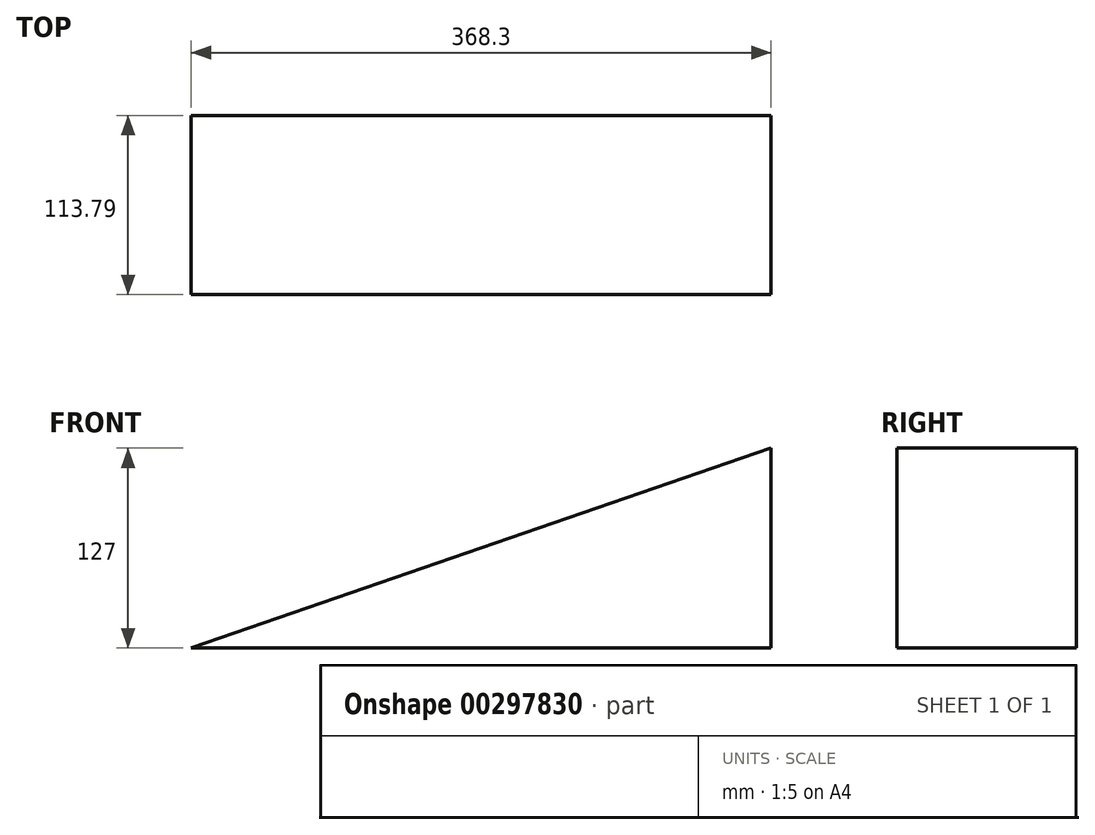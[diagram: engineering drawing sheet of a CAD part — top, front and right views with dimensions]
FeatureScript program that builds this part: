
annotation { "Feature Type Name" : "Feature", "Feature Type Description" : "" }
export const myFeature = defineFeature(function(context is Context, id is Id, definition is map)
    precondition{}
    {
        {
            var Q0;
            Q0=qCreatedBy(makeId("Front.planeOp"),FACE);
            var sketch = newSketch(context, id + "F0", { "sketchPlane" : qUnion([Q0])});
            skLineSegment(sketch, "E0", {"start": v(0, 0) * mm, "end": v(-368.3, 0) * mm});
            skLineSegment(sketch, "E1", {"start": v(0, 0) * mm, "end": v(0, 127) * mm});
            skLineSegment(sketch, "E2", {"start": v(0, 127) * mm, "end": v(-368.3, 0) * mm});
            skSolve(sketch);
        }
        {
            var Q0;
            Q0=makeQuery(id+"F0.imprint","IMPRINT",FACE,{"disambiguationData":[TD([[makeQuery(id+"F0.imprint","IMPRINT",EDGE,{"derivedFrom":sQuery(id+"F0.wireOp",EDGE,"E0")}),-1.0]])]});
            extrude(context, id + "F1", {"entities" : qUnion([Q0]), "depth" : 113.8 * mm});
        }
    });
